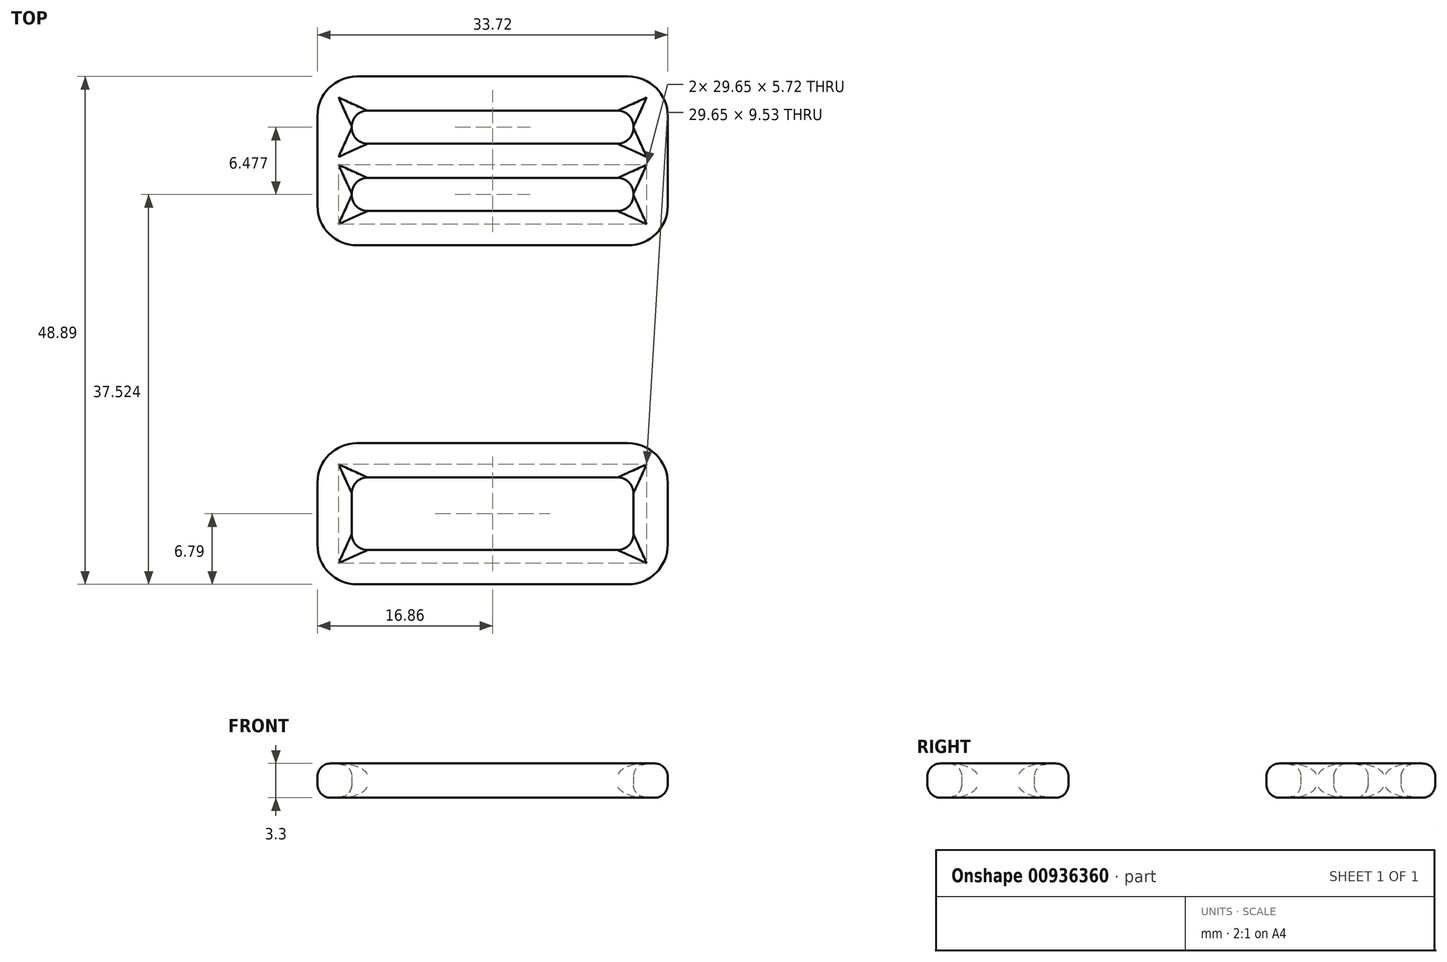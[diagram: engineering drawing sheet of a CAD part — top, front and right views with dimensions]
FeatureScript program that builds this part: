
annotation { "Feature Type Name" : "Feature", "Feature Type Description" : "" }
export const myFeature = defineFeature(function(context is Context, id is Id, definition is map)
    precondition{}
    {
        {
            var Q0;
            Q0=qCreatedBy(makeId("Top.planeOp"),FACE);
            var sketch = newSketch(context, id + "F0", { "sketchPlane" : qUnion([Q0])});
            skLineSegment(sketch, "E0.bottom", {"start": v(-13.56, 3.5) * mm, "end": v(13.56, 3.5) * mm});
            skLineSegment(sketch, "E0.top", {"start": v(-13.56, -3.5) * mm, "end": v(13.56, -3.5) * mm});
            skLineSegment(sketch, "E0.left", {"start": v(-13.56, 3.5) * mm, "end": v(-13.56, -3.5) * mm});
            skLineSegment(sketch, "E0.right", {"start": v(13.56, 3.5) * mm, "end": v(13.56, -3.5) * mm});
            skPoint(sketch, "E0.middle", {"position": v(0, 0) * mm});
            skLineSegment(sketch, "E1.bottom", {"start": v(-16.86, 6.8) * mm, "end": v(16.86, 6.8) * mm});
            skLineSegment(sketch, "E1.top", {"start": v(-16.86, -6.8) * mm, "end": v(16.86, -6.8) * mm});
            skLineSegment(sketch, "E1.left", {"start": v(-16.86, 6.8) * mm, "end": v(-16.86, -6.8) * mm});
            skLineSegment(sketch, "E1.right", {"start": v(16.86, 6.8) * mm, "end": v(16.86, -6.8) * mm});
            skLineSegment(sketch, "E2.bottom", {"start": v(-16.86, 25.84) * mm, "end": v(16.86, 25.84) * mm});
            skLineSegment(sketch, "E2.top", {"start": v(-16.86, 42.1) * mm, "end": v(16.86, 42.1) * mm});
            skLineSegment(sketch, "E2.left", {"start": v(-16.86, 25.84) * mm, "end": v(-16.86, 42.1) * mm});
            skLineSegment(sketch, "E2.right", {"start": v(16.86, 25.84) * mm, "end": v(16.86, 42.1) * mm});
            skPoint(sketch, "E2.middle", {"position": v(0, 33.97) * mm});
            skLineSegment(sketch, "E3.bottom", {"start": v(-13.56, 29.15) * mm, "end": v(13.56, 29.15) * mm});
            skLineSegment(sketch, "E3.top", {"start": v(-13.56, 38.8) * mm, "end": v(13.56, 38.8) * mm});
            skLineSegment(sketch, "E3.left", {"start": v(-13.56, 29.15) * mm, "end": v(-13.56, 38.8) * mm});
            skLineSegment(sketch, "E3.right", {"start": v(13.56, 29.15) * mm, "end": v(13.56, 38.8) * mm});
            skLineSegment(sketch, "E4.bottom", {"start": v(-13.56, 32.32) * mm, "end": v(13.56, 32.32) * mm});
            skLineSegment(sketch, "E4.top", {"start": v(-13.56, 35.62) * mm, "end": v(13.56, 35.62) * mm});
            skLineSegment(sketch, "E4.left", {"start": v(-13.56, 32.32) * mm, "end": v(-13.56, 35.62) * mm});
            skLineSegment(sketch, "E4.right", {"start": v(13.56, 32.32) * mm, "end": v(13.56, 35.62) * mm});
            skSolve(sketch);
        }
        {
            var Q0;
            Q0=makeQuery(id+"F0.imprint","IMPRINT",FACE,{"disambiguationData":[TD([[makeQuery(id+"F0.imprint","IMPRINT",EDGE,{"derivedFrom":sQuery(id+"F0.wireOp",EDGE,"E0.bottom")}),1.0]])]});
            var Q1;
            Q1=makeQuery(id+"F0.imprint","IMPRINT",FACE,{"disambiguationData":[TD([[makeQuery(id+"F0.imprint","IMPRINT",EDGE,{"derivedFrom":sQuery(id+"F0.wireOp",EDGE,"E2.bottom")}),1.0]])]});
            var Q2;
            Q2=makeQuery(id+"F0.imprint","IMPRINT",FACE,{"disambiguationData":[TD([[makeQuery(id+"F0.imprint","IMPRINT",EDGE,{"derivedFrom":sQuery(id+"F0.wireOp",EDGE,"E4.bottom")}),1.0]])]});
            extrude(context, id + "F1", {"entities" : qUnion([Q0, Q1, Q2]), "depth" : 3.3 * mm, "offsetDistance" : 25.4 * mm});
        }
        {
            var Q0;
            Q0=makeQuery(id+"F1.opExtrude","CAP_EDGE",EDGE,{"disambiguationData":[OSD([sQuery(id+"F0.wireOp",EDGE,"E0.bottom")])],"isStart":false});
            var Q1;
            Q1=makeQuery(id+"F1.opExtrude","CAP_EDGE",EDGE,{"disambiguationData":[OSD([sQuery(id+"F0.wireOp",EDGE,"E0.right")])],"isStart":false});
            var Q2;
            Q2=makeQuery(id+"F1.opExtrude","CAP_EDGE",EDGE,{"disambiguationData":[OSD([sQuery(id+"F0.wireOp",EDGE,"E0.top")])],"isStart":false});
            var Q3;
            Q3=makeQuery(id+"F1.opExtrude","CAP_EDGE",EDGE,{"disambiguationData":[OSD([sQuery(id+"F0.wireOp",EDGE,"E0.left")])],"isStart":false});
            var Q4;
            Q4=makeQuery(id+"F1.opExtrude","CAP_EDGE",EDGE,{"disambiguationData":[OSD([sQuery(id+"F0.wireOp",EDGE,"E1.left")])],"isStart":false});
            var Q5;
            Q5=makeQuery(id+"F1.opExtrude","CAP_EDGE",EDGE,{"disambiguationData":[OSD([sQuery(id+"F0.wireOp",EDGE,"E1.bottom")])],"isStart":false});
            var Q6;
            Q6=makeQuery(id+"F1.opExtrude","CAP_EDGE",EDGE,{"disambiguationData":[OSD([sQuery(id+"F0.wireOp",EDGE,"E1.right")])],"isStart":false});
            var Q7;
            Q7=makeQuery(id+"F1.opExtrude","CAP_EDGE",EDGE,{"disambiguationData":[OSD([sQuery(id+"F0.wireOp",EDGE,"E1.right")])],"isStart":true});
            var Q8;
            Q8=makeQuery(id+"F1.opExtrude","CAP_EDGE",EDGE,{"disambiguationData":[OSD([sQuery(id+"F0.wireOp",EDGE,"E1.top")])],"isStart":false});
            var Q9;
            Q9=makeQuery(id+"F1.opExtrude","CAP_EDGE",EDGE,{"disambiguationData":[OSD([sQuery(id+"F0.wireOp",EDGE,"E1.top")])],"isStart":true});
            var Q10;
            Q10=makeQuery(id+"F1.opExtrude","CAP_EDGE",EDGE,{"disambiguationData":[OSD([sQuery(id+"F0.wireOp",EDGE,"E1.left")])],"isStart":true});
            var Q11;
            Q11=makeQuery(id+"F1.opExtrude","CAP_EDGE",EDGE,{"disambiguationData":[OSD([sQuery(id+"F0.wireOp",EDGE,"E1.bottom")])],"isStart":true});
            var Q12;
            Q12=makeQuery(id+"F1.opExtrude","CAP_EDGE",EDGE,{"disambiguationData":[OSD([sQuery(id+"F0.wireOp",EDGE,"E0.top")])],"isStart":true});
            var Q13;
            Q13=makeQuery(id+"F1.opExtrude","CAP_EDGE",EDGE,{"disambiguationData":[OSD([sQuery(id+"F0.wireOp",EDGE,"E0.left")])],"isStart":true});
            var Q14;
            Q14=makeQuery(id+"F1.opExtrude","CAP_EDGE",EDGE,{"disambiguationData":[OSD([sQuery(id+"F0.wireOp",EDGE,"E0.bottom")])],"isStart":true});
            var Q15;
            Q15=makeQuery(id+"F1.opExtrude","CAP_EDGE",EDGE,{"disambiguationData":[OSD([sQuery(id+"F0.wireOp",EDGE,"E0.right")])],"isStart":true});
            var Q16;
            Q16=makeQuery(id+"F1.opExtrude","CAP_EDGE",EDGE,{"disambiguationData":[OSD([sQuery(id+"F0.wireOp",EDGE,"E3.top")])],"isStart":false});
            var Q17;
            Q17=makeQuery(id+"F1.opExtrude","CAP_EDGE",EDGE,{"disambiguationData":[OSD([sQuery(id+"F0.wireOp",EDGE,"E2.top")])],"isStart":false});
            var Q18;
            Q18=makeQuery(id+"F1.opExtrude","CAP_EDGE",EDGE,{"disambiguationData":[OSD([sQuery(id+"F0.wireOp",EDGE,"E2.left")])],"isStart":false});
            var Q19;
            Q19=makeQuery(id+"F1.opExtrude","CAP_EDGE",EDGE,{"disambiguationData":[OSD([sQuery(id+"F0.wireOp",EDGE,"E2.right")])],"isStart":false});
            var Q20;
            {var subQ0=sQuery(id+"F0.wireOp",EDGE,"E3.right");Q20=makeQuery(id+"F1.opExtrude","CAP_EDGE",EDGE,{"disambiguationData":[OSD([subQ0]),TDD([makeQuery(id+"F0.imprint","IMPRINT",EDGE,{"disambiguationData":[TD([[makeQuery(id+"F0.imprint","INTERSECT",VERTEX,{"derivedFrom":[sQuery(id+"F0.wireOp",EDGE,"E3.top"),subQ0]}),1.0]])],"derivedFrom":subQ0})])],"isStart":false});}
            var Q21;
            {var subQ0=sQuery(id+"F0.wireOp",EDGE,"E3.left");Q21=makeQuery(id+"F1.opExtrude","CAP_EDGE",EDGE,{"disambiguationData":[OSD([subQ0]),TDD([makeQuery(id+"F0.imprint","IMPRINT",EDGE,{"disambiguationData":[TD([[makeQuery(id+"F0.imprint","INTERSECT",VERTEX,{"derivedFrom":[sQuery(id+"F0.wireOp",EDGE,"E3.top"),subQ0]}),1.0]])],"derivedFrom":subQ0})])],"isStart":false});}
            var Q22;
            Q22=makeQuery(id+"F1.opExtrude","CAP_EDGE",EDGE,{"disambiguationData":[OSD([sQuery(id+"F0.wireOp",EDGE,"E4.top")])],"isStart":false});
            var Q23;
            Q23=makeQuery(id+"F1.opExtrude","CAP_EDGE",EDGE,{"disambiguationData":[OSD([sQuery(id+"F0.wireOp",EDGE,"E4.bottom")])],"isStart":false});
            var Q24;
            {var subQ0=sQuery(id+"F0.wireOp",EDGE,"E3.left");Q24=makeQuery(id+"F1.opExtrude","CAP_EDGE",EDGE,{"disambiguationData":[OSD([subQ0]),TDD([makeQuery(id+"F0.imprint","IMPRINT",EDGE,{"disambiguationData":[TD([[makeQuery(id+"F0.imprint","INTERSECT",VERTEX,{"derivedFrom":[sQuery(id+"F0.wireOp",EDGE,"E3.bottom"),subQ0]}),-1.0]])],"derivedFrom":subQ0})])],"isStart":false});}
            var Q25;
            {var subQ0=sQuery(id+"F0.wireOp",EDGE,"E3.right");Q25=makeQuery(id+"F1.opExtrude","CAP_EDGE",EDGE,{"disambiguationData":[OSD([subQ0]),TDD([makeQuery(id+"F0.imprint","IMPRINT",EDGE,{"disambiguationData":[TD([[makeQuery(id+"F0.imprint","INTERSECT",VERTEX,{"derivedFrom":[sQuery(id+"F0.wireOp",EDGE,"E3.bottom"),subQ0]}),-1.0]])],"derivedFrom":subQ0})])],"isStart":false});}
            var Q26;
            Q26=makeQuery(id+"F1.opExtrude","CAP_EDGE",EDGE,{"disambiguationData":[OSD([sQuery(id+"F0.wireOp",EDGE,"E3.bottom")])],"isStart":false});
            var Q27;
            Q27=makeQuery(id+"F1.opExtrude","CAP_EDGE",EDGE,{"disambiguationData":[OSD([sQuery(id+"F0.wireOp",EDGE,"E2.bottom")])],"isStart":false});
            var Q28;
            Q28=makeQuery(id+"F1.opExtrude","CAP_EDGE",EDGE,{"disambiguationData":[OSD([sQuery(id+"F0.wireOp",EDGE,"E2.bottom")])],"isStart":true});
            var Q29;
            Q29=makeQuery(id+"F1.opExtrude","CAP_EDGE",EDGE,{"disambiguationData":[OSD([sQuery(id+"F0.wireOp",EDGE,"E2.left")])],"isStart":true});
            var Q30;
            Q30=makeQuery(id+"F1.opExtrude","CAP_EDGE",EDGE,{"disambiguationData":[OSD([sQuery(id+"F0.wireOp",EDGE,"E3.bottom")])],"isStart":true});
            var Q31;
            {var subQ0=sQuery(id+"F0.wireOp",EDGE,"E3.left");Q31=makeQuery(id+"F1.opExtrude","CAP_EDGE",EDGE,{"disambiguationData":[OSD([subQ0]),TDD([makeQuery(id+"F0.imprint","IMPRINT",EDGE,{"disambiguationData":[TD([[makeQuery(id+"F0.imprint","INTERSECT",VERTEX,{"derivedFrom":[sQuery(id+"F0.wireOp",EDGE,"E3.bottom"),subQ0]}),-1.0]])],"derivedFrom":subQ0})])],"isStart":true});}
            var Q32;
            Q32=makeQuery(id+"F1.opExtrude","CAP_EDGE",EDGE,{"disambiguationData":[OSD([sQuery(id+"F0.wireOp",EDGE,"E4.bottom")])],"isStart":true});
            var Q33;
            {var subQ0=sQuery(id+"F0.wireOp",EDGE,"E3.right");Q33=makeQuery(id+"F1.opExtrude","CAP_EDGE",EDGE,{"disambiguationData":[OSD([subQ0]),TDD([makeQuery(id+"F0.imprint","IMPRINT",EDGE,{"disambiguationData":[TD([[makeQuery(id+"F0.imprint","INTERSECT",VERTEX,{"derivedFrom":[sQuery(id+"F0.wireOp",EDGE,"E3.bottom"),subQ0]}),-1.0]])],"derivedFrom":subQ0})])],"isStart":true});}
            var Q34;
            Q34=makeQuery(id+"F1.opExtrude","CAP_EDGE",EDGE,{"disambiguationData":[OSD([sQuery(id+"F0.wireOp",EDGE,"E2.right")])],"isStart":true});
            var Q35;
            Q35=makeQuery(id+"F1.opExtrude","CAP_EDGE",EDGE,{"disambiguationData":[OSD([sQuery(id+"F0.wireOp",EDGE,"E4.top")])],"isStart":true});
            var Q36;
            {var subQ0=sQuery(id+"F0.wireOp",EDGE,"E3.left");Q36=makeQuery(id+"F1.opExtrude","CAP_EDGE",EDGE,{"disambiguationData":[OSD([subQ0]),TDD([makeQuery(id+"F0.imprint","IMPRINT",EDGE,{"disambiguationData":[TD([[makeQuery(id+"F0.imprint","INTERSECT",VERTEX,{"derivedFrom":[sQuery(id+"F0.wireOp",EDGE,"E3.top"),subQ0]}),1.0]])],"derivedFrom":subQ0})])],"isStart":true});}
            var Q37;
            Q37=makeQuery(id+"F1.opExtrude","CAP_EDGE",EDGE,{"disambiguationData":[OSD([sQuery(id+"F0.wireOp",EDGE,"E3.top")])],"isStart":true});
            var Q38;
            {var subQ0=sQuery(id+"F0.wireOp",EDGE,"E3.right");Q38=makeQuery(id+"F1.opExtrude","CAP_EDGE",EDGE,{"disambiguationData":[OSD([subQ0]),TDD([makeQuery(id+"F0.imprint","IMPRINT",EDGE,{"disambiguationData":[TD([[makeQuery(id+"F0.imprint","INTERSECT",VERTEX,{"derivedFrom":[sQuery(id+"F0.wireOp",EDGE,"E3.top"),subQ0]}),1.0]])],"derivedFrom":subQ0})])],"isStart":true});}
            var Q39;
            Q39=makeQuery(id+"F1.opExtrude","CAP_EDGE",EDGE,{"disambiguationData":[OSD([sQuery(id+"F0.wireOp",EDGE,"E2.top")])],"isStart":true});
            fillet(context, id + "F2", {"entities" : qUnion([Q0, Q1, Q2, Q3, Q4, Q5, Q6, Q7, Q8, Q9, Q10, Q11, Q12, Q13, Q14, Q15, Q16, Q17, Q18, Q19, Q20, Q21, Q22, Q23, Q24, Q25, Q26, Q27, Q28, Q29, Q30, Q31, Q32, Q33, Q34, Q35, Q36, Q37, Q38, Q39]), "radius" : 1.27 * mm, "tangentPropagation" : true, "allowEdgeOverflow" : false});
        }
        {
            var Q0;
            Q0=makeQuery(id+"F1.opExtrude","SWEPT_EDGE",EDGE,{"disambiguationData":[OSD([sQuery(id+"F0.wireOp",EDGE,"E1.top"),sQuery(id+"F0.wireOp",EDGE,"E1.left")])]});
            var Q1;
            Q1=makeQuery(id+"F1.opExtrude","SWEPT_EDGE",EDGE,{"disambiguationData":[OSD([sQuery(id+"F0.wireOp",EDGE,"E1.top"),sQuery(id+"F0.wireOp",EDGE,"E1.right")])]});
            var Q2;
            Q2=makeQuery(id+"F1.opExtrude","SWEPT_EDGE",EDGE,{"disambiguationData":[OSD([sQuery(id+"F0.wireOp",EDGE,"E1.bottom"),sQuery(id+"F0.wireOp",EDGE,"E1.left")])]});
            var Q3;
            Q3=makeQuery(id+"F1.opExtrude","SWEPT_EDGE",EDGE,{"disambiguationData":[OSD([sQuery(id+"F0.wireOp",EDGE,"E1.bottom"),sQuery(id+"F0.wireOp",EDGE,"E1.right")])]});
            var Q4;
            Q4=makeQuery(id+"F1.opExtrude","SWEPT_EDGE",EDGE,{"disambiguationData":[OSD([sQuery(id+"F0.wireOp",EDGE,"E2.bottom"),sQuery(id+"F0.wireOp",EDGE,"E2.left")])]});
            var Q5;
            Q5=makeQuery(id+"F1.opExtrude","SWEPT_EDGE",EDGE,{"disambiguationData":[OSD([sQuery(id+"F0.wireOp",EDGE,"E2.bottom"),sQuery(id+"F0.wireOp",EDGE,"E2.right")])]});
            var Q6;
            Q6=makeQuery(id+"F1.opExtrude","SWEPT_EDGE",EDGE,{"disambiguationData":[OSD([sQuery(id+"F0.wireOp",EDGE,"E2.top"),sQuery(id+"F0.wireOp",EDGE,"E2.left")])]});
            var Q7;
            Q7=makeQuery(id+"F1.opExtrude","SWEPT_EDGE",EDGE,{"disambiguationData":[OSD([sQuery(id+"F0.wireOp",EDGE,"E2.top"),sQuery(id+"F0.wireOp",EDGE,"E2.right")])]});
            fillet(context, id + "F3", {"entities" : qUnion([Q0, Q1, Q2, Q3, Q4, Q5, Q6, Q7]), "radius" : 3.8 * mm, "tangentPropagation" : true, "allowEdgeOverflow" : false});
        }
        {
            var Q0;
            Q0=makeQuery(id+"F1.opExtrude","SWEPT_EDGE",EDGE,{"disambiguationData":[OSD([sQuery(id+"F0.wireOp",EDGE,"E0.bottom"),sQuery(id+"F0.wireOp",EDGE,"E0.right")])]});
            var Q1;
            Q1=makeQuery(id+"F1.opExtrude","SWEPT_EDGE",EDGE,{"disambiguationData":[OSD([sQuery(id+"F0.wireOp",EDGE,"E0.top"),sQuery(id+"F0.wireOp",EDGE,"E0.right")])]});
            var Q2;
            Q2=makeQuery(id+"F1.opExtrude","SWEPT_EDGE",EDGE,{"disambiguationData":[OSD([sQuery(id+"F0.wireOp",EDGE,"E0.bottom"),sQuery(id+"F0.wireOp",EDGE,"E0.left")])]});
            var Q3;
            Q3=makeQuery(id+"F1.opExtrude","SWEPT_EDGE",EDGE,{"disambiguationData":[OSD([sQuery(id+"F0.wireOp",EDGE,"E0.top"),sQuery(id+"F0.wireOp",EDGE,"E0.left")])]});
            var Q4;
            Q4=makeQuery(id+"F1.opExtrude","SWEPT_EDGE",EDGE,{"disambiguationData":[OSD([sQuery(id+"F0.wireOp",EDGE,"E3.top"),sQuery(id+"F0.wireOp",EDGE,"E3.left")])]});
            var Q5;
            Q5=makeQuery(id+"F1.opExtrude","SWEPT_EDGE",EDGE,{"disambiguationData":[OSD([sQuery(id+"F0.wireOp",EDGE,"E3.left"),sQuery(id+"F0.wireOp",EDGE,"E4.bottom"),sQuery(id+"F0.wireOp",EDGE,"E4.left")])]});
            var Q6;
            Q6=makeQuery(id+"F1.opExtrude","SWEPT_EDGE",EDGE,{"disambiguationData":[OSD([sQuery(id+"F0.wireOp",EDGE,"E3.top"),sQuery(id+"F0.wireOp",EDGE,"E3.right")])]});
            var Q7;
            Q7=makeQuery(id+"F1.opExtrude","SWEPT_EDGE",EDGE,{"disambiguationData":[OSD([sQuery(id+"F0.wireOp",EDGE,"E3.right"),sQuery(id+"F0.wireOp",EDGE,"E4.bottom"),sQuery(id+"F0.wireOp",EDGE,"E4.right")])]});
            var Q8;
            Q8=makeQuery(id+"F1.opExtrude","SWEPT_EDGE",EDGE,{"disambiguationData":[OSD([sQuery(id+"F0.wireOp",EDGE,"E3.right"),sQuery(id+"F0.wireOp",EDGE,"E4.top"),sQuery(id+"F0.wireOp",EDGE,"E4.right")])]});
            var Q9;
            Q9=makeQuery(id+"F1.opExtrude","SWEPT_EDGE",EDGE,{"disambiguationData":[OSD([sQuery(id+"F0.wireOp",EDGE,"E3.bottom"),sQuery(id+"F0.wireOp",EDGE,"E3.right")])]});
            var Q10;
            Q10=makeQuery(id+"F1.opExtrude","SWEPT_EDGE",EDGE,{"disambiguationData":[OSD([sQuery(id+"F0.wireOp",EDGE,"E3.bottom"),sQuery(id+"F0.wireOp",EDGE,"E3.left")])]});
            var Q11;
            Q11=makeQuery(id+"F1.opExtrude","SWEPT_EDGE",EDGE,{"disambiguationData":[OSD([sQuery(id+"F0.wireOp",EDGE,"E3.left"),sQuery(id+"F0.wireOp",EDGE,"E4.top"),sQuery(id+"F0.wireOp",EDGE,"E4.left")])]});
            fillet(context, id + "F4", {"entities" : qUnion([Q0, Q1, Q2, Q3, Q4, Q5, Q6, Q7, Q8, Q9, Q10, Q11]), "radius" : 1.52 * mm, "tangentPropagation" : true, "allowEdgeOverflow" : false});
        }
    });
